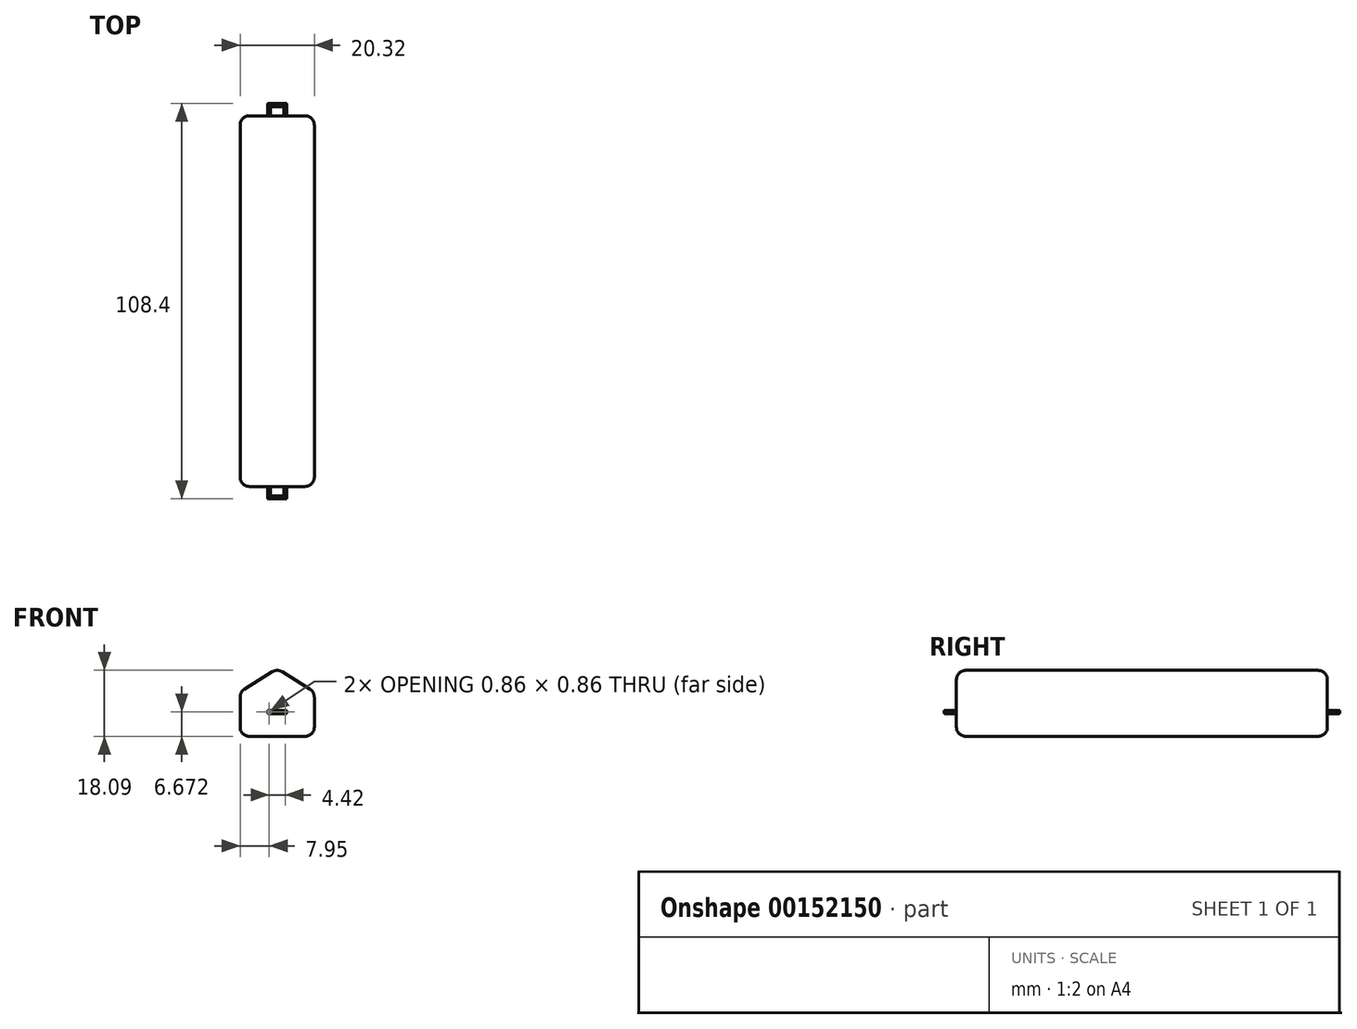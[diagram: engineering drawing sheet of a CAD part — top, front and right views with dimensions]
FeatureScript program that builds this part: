
annotation { "Feature Type Name" : "Feature", "Feature Type Description" : "" }
export const myFeature = defineFeature(function(context is Context, id is Id, definition is map)
    precondition{}
    {
        {
            var Q0;
            Q0=qCreatedBy(makeId("Front.planeOp"),FACE);
            var sketch = newSketch(context, id + "F0", { "sketchPlane" : qUnion([Q0])});
            skLineSegment(sketch, "E0", {"start": v(-10.16, -6.24) * mm, "end": v(-10.16, 5.96) * mm});
            skLineSegment(sketch, "E1", {"start": v(-10.16, 5.96) * mm, "end": v(0, 12.3) * mm});
            skLineSegment(sketch, "E2", {"start": v(-10.16, -6.24) * mm, "end": v(0, -6.24) * mm});
            skLineSegment(sketch, "E3", {"start": v(0, 12.3) * mm, "end": v(10.16, 5.96) * mm});
            skLineSegment(sketch, "E4", {"start": v(10.16, 5.96) * mm, "end": v(10.16, -6.24) * mm});
            skLineSegment(sketch, "E5", {"start": v(10.16, -6.24) * mm, "end": v(0, -6.24) * mm});
            skSolve(sketch);
        }
        {
            var Q0;
            Q0=makeQuery(id+"F0.imprint","IMPRINT",FACE,{"disambiguationData":[TD([[makeQuery(id+"F0.imprint","IMPRINT",EDGE,{"derivedFrom":sQuery(id+"F0.wireOp",EDGE,"E0")}),-1.0]])]});
            extrude(context, id + "F1", {"entities" : qUnion([Q0]), "depth" : 101.6 * mm});
        }
        {
            var Q0;
            Q0=makeQuery(id+"F1.opExtrude","SWEPT_EDGE",EDGE,{"disambiguationData":[OSD([sQuery(id+"F0.wireOp",EDGE,"E4"),sQuery(id+"F0.wireOp",EDGE,"E5")])]});
            var Q1;
            Q1=makeQuery(id+"F1.opExtrude","CAP_EDGE",EDGE,{"disambiguationData":[OSD([sQuery(id+"F0.wireOp",EDGE,"E2"),sQuery(id+"F0.wireOp",EDGE,"E5")])],"isStart":false});
            var Q2;
            Q2=makeQuery(id+"F1.opExtrude","SWEPT_EDGE",EDGE,{"disambiguationData":[OSD([sQuery(id+"F0.wireOp",EDGE,"E0"),sQuery(id+"F0.wireOp",EDGE,"E2")])]});
            var Q3;
            Q3=makeQuery(id+"F1.opExtrude","SWEPT_EDGE",EDGE,{"disambiguationData":[OSD([sQuery(id+"F0.wireOp",EDGE,"E3"),sQuery(id+"F0.wireOp",EDGE,"E4")])]});
            var Q4;
            Q4=makeQuery(id+"F1.opExtrude","CAP_EDGE",EDGE,{"disambiguationData":[OSD([sQuery(id+"F0.wireOp",EDGE,"E1")])],"isStart":false});
            var Q5;
            Q5=makeQuery(id+"F1.opExtrude","CAP_EDGE",EDGE,{"disambiguationData":[OSD([sQuery(id+"F0.wireOp",EDGE,"E0")])],"isStart":false});
            var Q6;
            Q6=makeQuery(id+"F1.opExtrude","CAP_EDGE",EDGE,{"disambiguationData":[OSD([sQuery(id+"F0.wireOp",EDGE,"E3")])],"isStart":false});
            var Q7;
            Q7=makeQuery(id+"F1.opExtrude","CAP_EDGE",EDGE,{"disambiguationData":[OSD([sQuery(id+"F0.wireOp",EDGE,"E4")])],"isStart":false});
            var Q8;
            Q8=makeQuery(id+"F1.opExtrude","SWEPT_EDGE",EDGE,{"disambiguationData":[OSD([sQuery(id+"F0.wireOp",EDGE,"E0"),sQuery(id+"F0.wireOp",EDGE,"E1")])]});
            var Q9;
            Q9=makeQuery(id+"F1.opExtrude","SWEPT_EDGE",EDGE,{"disambiguationData":[OSD([sQuery(id+"F0.wireOp",EDGE,"E1"),sQuery(id+"F0.wireOp",EDGE,"E3")])]});
            var Q10;
            Q10=makeQuery(id+"F1.opExtrude","CAP_EDGE",EDGE,{"disambiguationData":[OSD([sQuery(id+"F0.wireOp",EDGE,"E1")])],"isStart":true});
            var Q11;
            Q11=makeQuery(id+"F1.opExtrude","CAP_EDGE",EDGE,{"disambiguationData":[OSD([sQuery(id+"F0.wireOp",EDGE,"E3")])],"isStart":true});
            var Q12;
            Q12=makeQuery(id+"F1.opExtrude","CAP_EDGE",EDGE,{"disambiguationData":[OSD([sQuery(id+"F0.wireOp",EDGE,"E4")])],"isStart":true});
            var Q13;
            Q13=makeQuery(id+"F1.opExtrude","CAP_EDGE",EDGE,{"disambiguationData":[OSD([sQuery(id+"F0.wireOp",EDGE,"E2"),sQuery(id+"F0.wireOp",EDGE,"E5")])],"isStart":true});
            var Q14;
            Q14=makeQuery(id+"F1.opExtrude","CAP_EDGE",EDGE,{"disambiguationData":[OSD([sQuery(id+"F0.wireOp",EDGE,"E0")])],"isStart":true});
            fillet(context, id + "F2", {"entities" : qUnion([Q0, Q1, Q2, Q3, Q4, Q5, Q6, Q7, Q8, Q9, Q10, Q11, Q12, Q13, Q14]), "radius" : 2.54 * mm, "tangentPropagation" : true, "allowEdgeOverflow" : false});
        }
        {
            var Q0;
            Q0=makeQuery(id+"F1.opExtrude","CAP_FACE",FACE,{"disambiguationData":[OSD([sQuery(id+"F0.wireOp",EDGE,"E0"),sQuery(id+"F0.wireOp",EDGE,"E1"),sQuery(id+"F0.wireOp",EDGE,"E2"),sQuery(id+"F0.wireOp",EDGE,"E3"),sQuery(id+"F0.wireOp",EDGE,"E4"),sQuery(id+"F0.wireOp",EDGE,"E5")])],"isStart":false});
            var sketch = newSketch(context, id + "F3", { "sketchPlane" : qUnion([Q0])});
            skLineSegment(sketch, "E6.bottom", {"start": v(1.78, 0) * mm, "end": v(2.64, 0) * mm});
            skLineSegment(sketch, "E6.top", {"start": v(1.78, 0.86) * mm, "end": v(2.64, 0.86) * mm});
            skLineSegment(sketch, "E6.left", {"start": v(1.78, 0) * mm, "end": v(1.78, 0.86) * mm});
            skLineSegment(sketch, "E6.right", {"start": v(2.64, 0) * mm, "end": v(2.64, 0.86) * mm});
            skLineSegment(sketch, "E7.bottom", {"start": v(-1.78, 0) * mm, "end": v(-2.64, 0) * mm});
            skLineSegment(sketch, "E7.top", {"start": v(-1.78, 0.86) * mm, "end": v(-2.64, 0.86) * mm});
            skLineSegment(sketch, "E7.left", {"start": v(-1.78, 0) * mm, "end": v(-1.78, 0.86) * mm});
            skLineSegment(sketch, "E7.right", {"start": v(-2.64, 0) * mm, "end": v(-2.64, 0.86) * mm});
            skSolve(sketch);
        }
        {
            var Q0;
            Q0 = qSketchRegion(id + "F3", true);
            extrude(context, id + "F4", {"entities" : qUnion([Q0]), "operationType" : NewBodyOperationType.ADD, "depth" : 2.54 * mm});
        }
        {
            var Q0;
            Q0=makeQuery(id+"F4.opExtrude","CAP_FACE",FACE,{"disambiguationData":[OSD([sQuery(id+"F3.wireOp",EDGE,"E6.bottom"),sQuery(id+"F3.wireOp",EDGE,"E6.top"),sQuery(id+"F3.wireOp",EDGE,"E6.left"),sQuery(id+"F3.wireOp",EDGE,"E6.right")])],"isStart":false});
            var sketch = newSketch(context, id + "F5", { "sketchPlane" : qUnion([Q0])});
            skLineSegment(sketch, "E8.bottom", {"start": v(2.64, 0) * mm, "end": v(-2.64, 0) * mm});
            skLineSegment(sketch, "E8.top", {"start": v(2.64, 0.86) * mm, "end": v(-2.64, 0.86) * mm});
            skLineSegment(sketch, "E8.left", {"start": v(2.64, 0) * mm, "end": v(2.64, 0.86) * mm});
            skLineSegment(sketch, "E8.right", {"start": v(-2.64, 0) * mm, "end": v(-2.64, 0.86) * mm});
            skSolve(sketch);
        }
        {
            var Q0;
            Q0 = qSketchRegion(id + "F5", true);
            extrude(context, id + "F6", {"entities" : qUnion([Q0]), "operationType" : NewBodyOperationType.ADD, "depth" : 0.86 * mm});
        }
        {
            var Q0;
            Q0=makeQuery(id+"F4.opExtrude","SWEPT_EDGE",EDGE,{"disambiguationData":[OSD([sQuery(id+"F3.wireOp",EDGE,"E7.top"),sQuery(id+"F3.wireOp",EDGE,"E7.left")])]});
            var Q1;
            Q1=makeQuery(id+"F4.opExtrude","SWEPT_EDGE",EDGE,{"disambiguationData":[OSD([sQuery(id+"F3.wireOp",EDGE,"E7.top"),sQuery(id+"F3.wireOp",EDGE,"E7.right")])]});
            var Q2;
            Q2=makeQuery(id+"F6.opExtrude","CAP_EDGE",EDGE,{"disambiguationData":[OSD([sQuery(id+"F5.wireOp",EDGE,"E8.bottom")])],"isStart":false});
            var Q3;
            Q3=makeQuery(id+"F6.opExtrude","CAP_EDGE",EDGE,{"disambiguationData":[OSD([sQuery(id+"F5.wireOp",EDGE,"E8.top")])],"isStart":false});
            var Q4;
            Q4=makeQuery(id+"F6.boolean.opBoolean","MERGE",EDGE,{"derivedFrom":[makeQuery(id+"F4.opExtrude","CAP_EDGE",EDGE,{"disambiguationData":[OSD([sQuery(id+"F3.wireOp",EDGE,"E7.right")])],"isStart":false}),makeQuery(id+"F6.opExtrude","CAP_EDGE",EDGE,{"disambiguationData":[OSD([sQuery(id+"F5.wireOp",EDGE,"E8.right")])],"isStart":true})]});
            var Q5;
            Q5=makeQuery(id+"F6.opExtrude","SWEPT_EDGE",EDGE,{"disambiguationData":[OSD([sQuery(id+"F5.wireOp",EDGE,"E8.top"),sQuery(id+"F5.wireOp",EDGE,"E8.right")])]});
            var Q6;
            Q6=makeQuery(id+"F6.opExtrude","CAP_EDGE",EDGE,{"disambiguationData":[OSD([sQuery(id+"F5.wireOp",EDGE,"E8.right")])],"isStart":false});
            var Q7;
            Q7=makeQuery(id+"F6.opExtrude","SWEPT_EDGE",EDGE,{"disambiguationData":[OSD([sQuery(id+"F5.wireOp",EDGE,"E8.bottom"),sQuery(id+"F5.wireOp",EDGE,"E8.right")])]});
            var Q8;
            Q8=makeQuery(id+"F4.opExtrude","SWEPT_EDGE",EDGE,{"disambiguationData":[OSD([sQuery(id+"F3.wireOp",EDGE,"E7.bottom"),sQuery(id+"F3.wireOp",EDGE,"E7.right")])]});
            var Q9;
            Q9=makeQuery(id+"F6.opExtrude","CAP_EDGE",EDGE,{"disambiguationData":[OSD([sQuery(id+"F5.wireOp",EDGE,"E8.top")])],"isStart":true});
            var Q10;
            Q10=makeQuery(id+"F4.opExtrude","SWEPT_EDGE",EDGE,{"disambiguationData":[OSD([sQuery(id+"F3.wireOp",EDGE,"E6.bottom"),sQuery(id+"F3.wireOp",EDGE,"E6.left")])]});
            var Q11;
            Q11=makeQuery(id+"F4.opExtrude","SWEPT_EDGE",EDGE,{"disambiguationData":[OSD([sQuery(id+"F3.wireOp",EDGE,"E6.top"),sQuery(id+"F3.wireOp",EDGE,"E6.left")])]});
            var Q12;
            Q12=makeQuery(id+"F6.boolean.opBoolean","MERGE",EDGE,{"derivedFrom":[makeQuery(id+"F4.opExtrude","SWEPT_EDGE",EDGE,{"disambiguationData":[OSD([sQuery(id+"F3.wireOp",EDGE,"E6.top"),sQuery(id+"F3.wireOp",EDGE,"E6.right")])]}),makeQuery(id+"F6.opExtrude","SWEPT_EDGE",EDGE,{"disambiguationData":[OSD([sQuery(id+"F5.wireOp",EDGE,"E8.top"),sQuery(id+"F5.wireOp",EDGE,"E8.left")])]})]});
            var Q13;
            Q13=makeQuery(id+"F6.opExtrude","CAP_EDGE",EDGE,{"disambiguationData":[OSD([sQuery(id+"F5.wireOp",EDGE,"E8.left")])],"isStart":false});
            var Q14;
            Q14=makeQuery(id+"F6.boolean.opBoolean","MERGE",EDGE,{"derivedFrom":[makeQuery(id+"F4.opExtrude","SWEPT_EDGE",EDGE,{"disambiguationData":[OSD([sQuery(id+"F3.wireOp",EDGE,"E6.bottom"),sQuery(id+"F3.wireOp",EDGE,"E6.right")])]}),makeQuery(id+"F6.opExtrude","SWEPT_EDGE",EDGE,{"disambiguationData":[OSD([sQuery(id+"F5.wireOp",EDGE,"E8.bottom"),sQuery(id+"F5.wireOp",EDGE,"E8.left")])]})]});
            var Q15;
            Q15=makeQuery(id+"F4.opExtrude","SWEPT_EDGE",EDGE,{"disambiguationData":[OSD([sQuery(id+"F3.wireOp",EDGE,"E7.bottom"),sQuery(id+"F3.wireOp",EDGE,"E7.left")])]});
            var Q16;
            Q16=makeQuery(id+"F6.opExtrude","CAP_EDGE",EDGE,{"disambiguationData":[OSD([sQuery(id+"F5.wireOp",EDGE,"E8.bottom")])],"isStart":true});
            var Q17;
            Q17=makeQuery(id+"F4.opExtrude","CAP_EDGE",EDGE,{"disambiguationData":[OSD([sQuery(id+"F3.wireOp",EDGE,"E7.left")])],"isStart":false});
            var Q18;
            Q18=makeQuery(id+"F4.opExtrude","CAP_EDGE",EDGE,{"disambiguationData":[OSD([sQuery(id+"F3.wireOp",EDGE,"E6.left")])],"isStart":false});
            fillet(context, id + "F7", {"entities" : qUnion([Q0, Q1, Q2, Q3, Q4, Q5, Q6, Q7, Q8, Q9, Q10, Q11, Q12, Q13, Q14, Q15, Q16, Q17, Q18]), "radius" : 0.25 * mm, "tangentPropagation" : true, "allowEdgeOverflow" : false});
        }
        {
            var Q0;
            Q0=makeQuery(id+"F1.opExtrude","CAP_FACE",FACE,{"disambiguationData":[OSD([sQuery(id+"F0.wireOp",EDGE,"E0"),sQuery(id+"F0.wireOp",EDGE,"E1"),sQuery(id+"F0.wireOp",EDGE,"E2"),sQuery(id+"F0.wireOp",EDGE,"E3"),sQuery(id+"F0.wireOp",EDGE,"E4"),sQuery(id+"F0.wireOp",EDGE,"E5")])],"isStart":true});
            var sketch = newSketch(context, id + "F8", { "sketchPlane" : qUnion([Q0])});
            skLineSegment(sketch, "E9.bottom", {"start": v(-1.78, 0) * mm, "end": v(-2.64, 0) * mm});
            skLineSegment(sketch, "E9.top", {"start": v(-1.78, 0.86) * mm, "end": v(-2.64, 0.86) * mm});
            skLineSegment(sketch, "E9.left", {"start": v(-1.78, 0) * mm, "end": v(-1.78, 0.86) * mm});
            skLineSegment(sketch, "E9.right", {"start": v(-2.64, 0) * mm, "end": v(-2.64, 0.86) * mm});
            skLineSegment(sketch, "E10.bottom", {"start": v(1.78, 0) * mm, "end": v(2.64, 0) * mm});
            skLineSegment(sketch, "E10.top", {"start": v(1.78, 0.86) * mm, "end": v(2.64, 0.86) * mm});
            skLineSegment(sketch, "E10.left", {"start": v(1.78, 0) * mm, "end": v(1.78, 0.86) * mm});
            skLineSegment(sketch, "E10.right", {"start": v(2.64, 0) * mm, "end": v(2.64, 0.86) * mm});
            skSolve(sketch);
        }
        {
            var Q0;
            Q0 = qSketchRegion(id + "F8", true);
            extrude(context, id + "F9", {"entities" : qUnion([Q0]), "operationType" : NewBodyOperationType.ADD, "depth" : 2.54 * mm});
        }
        {
            var Q0;
            Q0=makeQuery(id+"F9.opExtrude","CAP_FACE",FACE,{"disambiguationData":[OSD([sQuery(id+"F8.wireOp",EDGE,"E9.bottom"),sQuery(id+"F8.wireOp",EDGE,"E9.top"),sQuery(id+"F8.wireOp",EDGE,"E9.left"),sQuery(id+"F8.wireOp",EDGE,"E9.right")])],"isStart":false});
            var sketch = newSketch(context, id + "F10", { "sketchPlane" : qUnion([Q0])});
            skLineSegment(sketch, "E11.bottom", {"start": v(-2.64, 0.86) * mm, "end": v(2.64, 0.86) * mm});
            skLineSegment(sketch, "E11.top", {"start": v(-2.64, 0) * mm, "end": v(2.64, 0) * mm});
            skLineSegment(sketch, "E11.left", {"start": v(-2.64, 0.86) * mm, "end": v(-2.64, 0) * mm});
            skLineSegment(sketch, "E11.right", {"start": v(2.64, 0.86) * mm, "end": v(2.64, 0) * mm});
            skSolve(sketch);
        }
        {
            var Q0;
            Q0 = qSketchRegion(id + "F10", true);
            extrude(context, id + "F11", {"entities" : qUnion([Q0]), "operationType" : NewBodyOperationType.ADD, "depth" : 0.86 * mm});
        }
        {
            var Q0;
            Q0=makeQuery(id+"F9.opExtrude","SWEPT_EDGE",EDGE,{"disambiguationData":[OSD([sQuery(id+"F8.wireOp",EDGE,"E10.top"),sQuery(id+"F8.wireOp",EDGE,"E10.left")])]});
            var Q1;
            Q1=makeQuery(id+"F9.opExtrude","SWEPT_EDGE",EDGE,{"disambiguationData":[OSD([sQuery(id+"F8.wireOp",EDGE,"E10.bottom"),sQuery(id+"F8.wireOp",EDGE,"E10.left")])]});
            var Q2;
            Q2=makeQuery(id+"F9.opExtrude","SWEPT_EDGE",EDGE,{"disambiguationData":[OSD([sQuery(id+"F8.wireOp",EDGE,"E9.top"),sQuery(id+"F8.wireOp",EDGE,"E9.left")])]});
            var Q3;
            Q3=makeQuery(id+"F11.boolean.opBoolean","MERGE",EDGE,{"derivedFrom":[makeQuery(id+"F9.opExtrude","SWEPT_EDGE",EDGE,{"disambiguationData":[OSD([sQuery(id+"F8.wireOp",EDGE,"E9.top"),sQuery(id+"F8.wireOp",EDGE,"E9.right")])]}),makeQuery(id+"F11.opExtrude","SWEPT_EDGE",EDGE,{"disambiguationData":[OSD([sQuery(id+"F10.wireOp",EDGE,"E11.bottom"),sQuery(id+"F10.wireOp",EDGE,"E11.left")])]})]});
            var Q4;
            Q4=makeQuery(id+"F11.boolean.opBoolean","MERGE",EDGE,{"derivedFrom":[makeQuery(id+"F9.opExtrude","SWEPT_EDGE",EDGE,{"disambiguationData":[OSD([sQuery(id+"F8.wireOp",EDGE,"E9.bottom"),sQuery(id+"F8.wireOp",EDGE,"E9.right")])]}),makeQuery(id+"F11.opExtrude","SWEPT_EDGE",EDGE,{"disambiguationData":[OSD([sQuery(id+"F10.wireOp",EDGE,"E11.top"),sQuery(id+"F10.wireOp",EDGE,"E11.left")])]})]});
            var Q5;
            Q5=makeQuery(id+"F11.opExtrude","CAP_EDGE",EDGE,{"disambiguationData":[OSD([sQuery(id+"F10.wireOp",EDGE,"E11.bottom")])],"isStart":true});
            var Q6;
            Q6=makeQuery(id+"F11.opExtrude","CAP_EDGE",EDGE,{"disambiguationData":[OSD([sQuery(id+"F10.wireOp",EDGE,"E11.bottom")])],"isStart":false});
            var Q7;
            Q7=makeQuery(id+"F11.opExtrude","CAP_EDGE",EDGE,{"disambiguationData":[OSD([sQuery(id+"F10.wireOp",EDGE,"E11.top")])],"isStart":false});
            var Q8;
            Q8=makeQuery(id+"F11.opExtrude","CAP_EDGE",EDGE,{"disambiguationData":[OSD([sQuery(id+"F10.wireOp",EDGE,"E11.left")])],"isStart":false});
            var Q9;
            Q9=makeQuery(id+"F11.opExtrude","CAP_EDGE",EDGE,{"disambiguationData":[OSD([sQuery(id+"F10.wireOp",EDGE,"E11.right")])],"isStart":false});
            var Q10;
            Q10=makeQuery(id+"F9.opExtrude","SWEPT_EDGE",EDGE,{"disambiguationData":[OSD([sQuery(id+"F8.wireOp",EDGE,"E10.top"),sQuery(id+"F8.wireOp",EDGE,"E10.right")])]});
            var Q11;
            Q11=makeQuery(id+"F11.opExtrude","SWEPT_EDGE",EDGE,{"disambiguationData":[OSD([sQuery(id+"F10.wireOp",EDGE,"E11.bottom"),sQuery(id+"F10.wireOp",EDGE,"E11.right")])]});
            var Q12;
            Q12=makeQuery(id+"F11.opExtrude","SWEPT_EDGE",EDGE,{"disambiguationData":[OSD([sQuery(id+"F10.wireOp",EDGE,"E11.top"),sQuery(id+"F10.wireOp",EDGE,"E11.right")])]});
            var Q13;
            Q13=makeQuery(id+"F9.opExtrude","SWEPT_EDGE",EDGE,{"disambiguationData":[OSD([sQuery(id+"F8.wireOp",EDGE,"E10.bottom"),sQuery(id+"F8.wireOp",EDGE,"E10.right")])]});
            var Q14;
            Q14=makeQuery(id+"F9.opExtrude","SWEPT_EDGE",EDGE,{"disambiguationData":[OSD([sQuery(id+"F8.wireOp",EDGE,"E9.bottom"),sQuery(id+"F8.wireOp",EDGE,"E9.left")])]});
            var Q15;
            Q15=makeQuery(id+"F11.opExtrude","CAP_EDGE",EDGE,{"disambiguationData":[OSD([sQuery(id+"F10.wireOp",EDGE,"E11.top")])],"isStart":true});
            var Q16;
            Q16=makeQuery(id+"F9.opExtrude","CAP_EDGE",EDGE,{"disambiguationData":[OSD([sQuery(id+"F8.wireOp",EDGE,"E10.left")])],"isStart":false});
            var Q17;
            Q17=makeQuery(id+"F9.opExtrude","CAP_EDGE",EDGE,{"disambiguationData":[OSD([sQuery(id+"F8.wireOp",EDGE,"E9.left")])],"isStart":false});
            fillet(context, id + "F12", {"entities" : qUnion([Q0, Q1, Q2, Q3, Q4, Q5, Q6, Q7, Q8, Q9, Q10, Q11, Q12, Q13, Q14, Q15, Q16, Q17]), "radius" : 0.25 * mm, "tangentPropagation" : true, "allowEdgeOverflow" : false});
        }
    });
